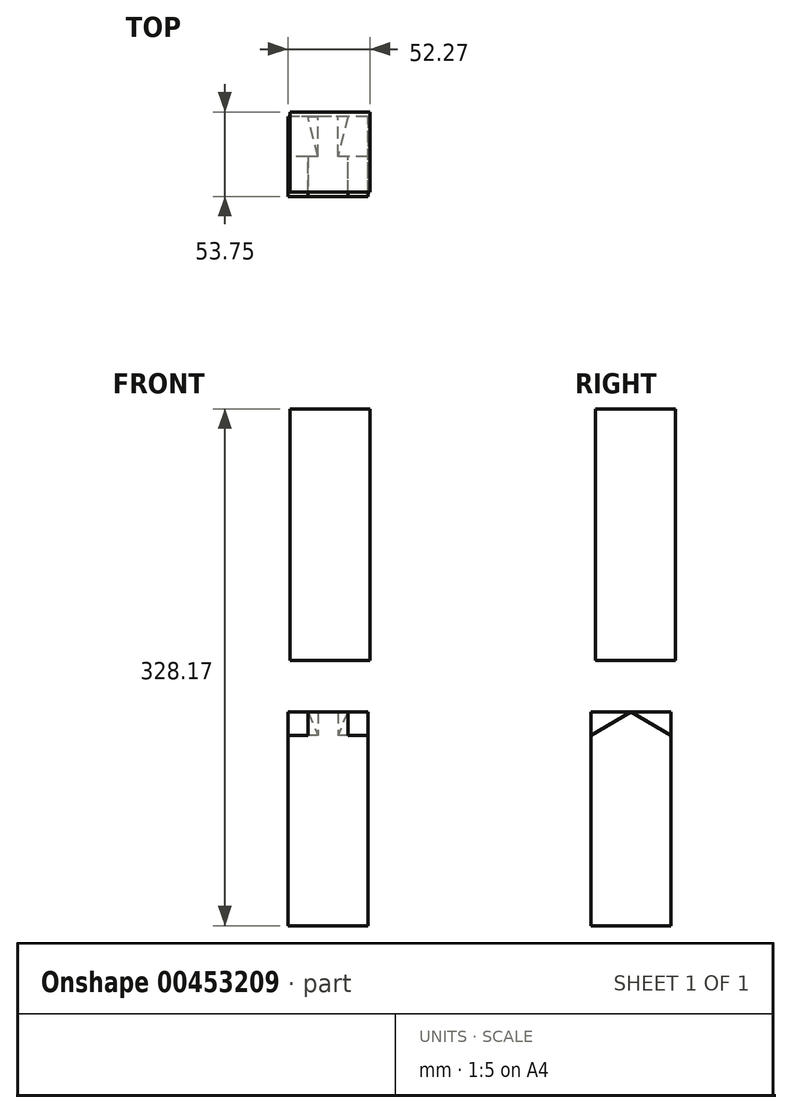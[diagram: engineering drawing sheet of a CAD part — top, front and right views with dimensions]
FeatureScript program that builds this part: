
annotation { "Feature Type Name" : "Feature", "Feature Type Description" : "" }
export const myFeature = defineFeature(function(context is Context, id is Id, definition is map)
    precondition{}
    {
        {
            var Q0;
            Q0=qCreatedBy(makeId("Top.planeOp"),FACE);
            var sketch = newSketch(context, id + "F0", { "sketchPlane" : qUnion([Q0])});
            skLineSegment(sketch, "E0.bottom", {"start": v(30.23, -20.65) * mm, "end": v(-20.57, -20.65) * mm});
            skLineSegment(sketch, "E0.top", {"start": v(30.23, 30.15) * mm, "end": v(-20.57, 30.15) * mm});
            skLineSegment(sketch, "E0.left", {"start": v(30.23, -20.65) * mm, "end": v(30.23, 30.15) * mm});
            skLineSegment(sketch, "E0.right", {"start": v(-20.57, -20.65) * mm, "end": v(-20.57, 30.15) * mm});
            skSolve(sketch);
        }
        {
            var Q0;
            Q0=makeQuery(id+"F0.imprint","IMPRINT",FACE,{"disambiguationData":[TD([[makeQuery(id+"F0.imprint","IMPRINT",EDGE,{"derivedFrom":sQuery(id+"F0.wireOp",EDGE,"E0.bottom")}),-1.0]])]});
            extrude(context, id + "F1", {"entities" : qUnion([Q0]), "depth" : 135.89 * mm});
        }
        {
            var Q0;
            Q0=makeQuery(id+"F1.opExtrude","SWEPT_FACE",FACE,{"disambiguationData":[OSD([sQuery(id+"F0.wireOp",EDGE,"E0.top")])]});
            var sketch = newSketch(context, id + "F2", { "sketchPlane" : qUnion([Q0])});
            skLineSegment(sketch, "E1", {"start": v(-17.53, 135.9) * mm, "end": v(-11.18, 120.72) * mm});
            skLineSegment(sketch, "E2", {"start": v(7.87, 135.9) * mm, "end": v(1.52, 120.72) * mm});
            skLineSegment(sketch, "E3", {"start": v(-11.18, 120.72) * mm, "end": v(1.52, 120.72) * mm});
            skLineSegment(sketch, "E4", {"start": v(-11.18, 120.72) * mm, "end": v(-30.23, 120.72) * mm});
            skLineSegment(sketch, "E5", {"start": v(1.52, 120.72) * mm, "end": v(20.57, 120.72) * mm});
            skSolve(sketch);
        }
        {
            var Q0;
            Q0=makeQuery(id+"F1.opExtrude","SWEPT_FACE",FACE,{"disambiguationData":[OSD([sQuery(id+"F0.wireOp",EDGE,"E0.right")])]});
            var sketch = newSketch(context, id + "F3", { "sketchPlane" : qUnion([Q0])});
            skLineSegment(sketch, "E6", {"start": v(-30.15, 120.72) * mm, "end": v(-4.75, 135.9) * mm});
            skLineSegment(sketch, "E7", {"start": v(-4.75, 135.9) * mm, "end": v(20.65, 120.72) * mm});
            skSolve(sketch);
        }
        {
            var Q0;
            Q0=makeQuery(id+"F1.opExtrude","CAP_FACE",FACE,{"disambiguationData":[OSD([sQuery(id+"F0.wireOp",EDGE,"E0.bottom"),sQuery(id+"F0.wireOp",EDGE,"E0.top"),sQuery(id+"F0.wireOp",EDGE,"E0.left"),sQuery(id+"F0.wireOp",EDGE,"E0.right")])],"isStart":false});
            var sketch = newSketch(context, id + "F4", { "sketchPlane" : qUnion([Q0])});
            skLineSegment(sketch, "E8", {"start": v(-7.87, 30.15) * mm, "end": v(-7.87, -20.65) * mm});
            skLineSegment(sketch, "E9", {"start": v(17.53, 30.15) * mm, "end": v(17.53, -20.65) * mm});
            skLineSegment(sketch, "E10", {"start": v(-20.57, 4.75) * mm, "end": v(30.23, 4.75) * mm});
            skLineSegment(sketch, "E11", {"start": v(17.53, 30.15) * mm, "end": v(11.18, 4.75) * mm});
            skLineSegment(sketch, "E12", {"start": v(11.18, 4.75) * mm, "end": v(-1.52, 4.75) * mm});
            skLineSegment(sketch, "E13", {"start": v(-1.52, 4.75) * mm, "end": v(-7.87, 30.15) * mm});
            skLineSegment(sketch, "E14", {"start": v(11.18, 4.75) * mm, "end": v(30.23, 4.75) * mm});
            skLineSegment(sketch, "E15", {"start": v(-1.52, 4.75) * mm, "end": v(-20.57, 4.75) * mm});
            skSolve(sketch);
        }
        {
            var Q0;
            {var subQ4=sQuery(id+"F3.wireOp",EDGE,"E6");Q0=makeQuery(id+"F3.imprint","IMPRINT",FACE,{"disambiguationData":[TD([[makeQuery(id+"F3.imprint","IMPRINT",EDGE,{"derivedFrom":subQ4}),-1.0]])]});}
            var sketch = newSketch(context, id + "F5", { "sketchPlane" : qUnion([Q0])});
            skLineSegment(sketch, "E16", {"start": v(-4.75, 135.9) * mm, "end": v(-4.75, 120.72) * mm});
            skLineSegment(sketch, "E17", {"start": v(-4.75, 120.72) * mm, "end": v(-30.15, 120.72) * mm});
            skLineSegment(sketch, "E18", {"start": v(-4.75, 135.9) * mm, "end": v(-30.15, 120.72) * mm});
            skSolve(sketch);
        }
        {
            var Q0;
            Q0=qSketchRegion(id+"F5",true);
            var Q1;
            {var subQ0=sQuery(id+"F3.wireOp",EDGE,"E6");Q1=makeQuery(id+"F3.imprint","IMPRINT",FACE,{"disambiguationData":[TD([[makeQuery(id+"F3.imprint","IMPRINT",EDGE,{"derivedFrom":subQ0}),1.0]])]});}
            extrude(context, id + "F6", {"entities" : qUnion([Q0, Q1]), "operationType" : NewBodyOperationType.REMOVE, "oppositeDirection" : true, "depth" : 50.8 * mm});
        }
        {
            var Q0;
            Q0=makeQuery(id+"F6.boolean.opBoolean","COPY",FACE,{"derivedFrom":makeQuery(id+"F6.opExtrude","SWEPT_FACE",FACE,{"disambiguationData":[OSD([sQuery(id+"F5.wireOp",EDGE,"E16")])]})});
            var sketch = newSketch(context, id + "F7", { "sketchPlane" : qUnion([Q0])});
            skLineSegment(sketch, "E19", {"start": v(-11.18, 135.9) * mm, "end": v(-11.18, 120.72) * mm});
            skSolve(sketch);
        }
        {
            var Q0;
            Q0=makeQuery(id+"F6.boolean.opBoolean","COPY",FACE,{"derivedFrom":makeQuery(id+"F6.opExtrude","SWEPT_FACE",FACE,{"disambiguationData":[OSD([sQuery(id+"F5.wireOp",EDGE,"E17")])]})});
            var sketch = newSketch(context, id + "F8", { "sketchPlane" : qUnion([Q0])});
            skLineSegment(sketch, "E20", {"start": v(11.18, 30.15) * mm, "end": v(11.18, 4.75) * mm});
            skSolve(sketch);
        }
        {
            var Q0;
            {var subQ0=sQuery(id+"F7.wireOp",EDGE,"E19");Q0=makeQuery(id+"F7.imprint","IMPRINT",FACE,{"disambiguationData":[TD([[makeQuery(id+"F7.imprint","IMPRINT",EDGE,{"derivedFrom":subQ0}),1.0]])]});}
            var sketch = newSketch(context, id + "F9", { "sketchPlane" : qUnion([Q0])});
            skLineSegment(sketch, "E21", {"start": v(1.52, 135.9) * mm, "end": v(1.52, 120.72) * mm});
            skSolve(sketch);
        }
        {
            var Q0;
            {var subQ0=sQuery(id+"F8.wireOp",EDGE,"E20");Q0=makeQuery(id+"F8.imprint","IMPRINT",FACE,{"disambiguationData":[TD([[makeQuery(id+"F8.imprint","IMPRINT",EDGE,{"derivedFrom":subQ0}),-1.0]])]});}
            var sketch = newSketch(context, id + "F10", { "sketchPlane" : qUnion([Q0])});
            skLineSegment(sketch, "E22", {"start": v(-1.52, 4.75) * mm, "end": v(-1.52, 30.15) * mm});
            skSolve(sketch);
        }
        {
            var Q0;
            {var subQ0=sQuery(id+"F2.wireOp",EDGE,"E1");Q0=makeQuery(id+"F2.imprint","IMPRINT",FACE,{"disambiguationData":[TD([[makeQuery(id+"F2.imprint","IMPRINT",EDGE,{"derivedFrom":subQ0}),1.0]])]});}
            var sketch = newSketch(context, id + "F11", { "sketchPlane" : qUnion([Q0])});
            skLineSegment(sketch, "E23", {"start": v(-11.18, 135.9) * mm, "end": v(1.52, 135.9) * mm});
            skLineSegment(sketch, "E24", {"start": v(1.52, 135.9) * mm, "end": v(1.52, 120.72) * mm});
            skLineSegment(sketch, "E25", {"start": v(1.52, 120.72) * mm, "end": v(-11.18, 120.72) * mm});
            skLineSegment(sketch, "E26", {"start": v(-11.18, 120.72) * mm, "end": v(-11.18, 135.9) * mm});
            skSolve(sketch);
        }
        {
            var Q0;
            Q0=makeQuery(id+"F11.imprint","IMPRINT",FACE,{"disambiguationData":[TD([[makeQuery(id+"F11.imprint","IMPRINT",EDGE,{"derivedFrom":sQuery(id+"F11.wireOp",EDGE,"E23")}),-1.0]])]});
            extrude(context, id + "F12", {"entities" : qUnion([Q0]), "operationType" : NewBodyOperationType.ADD, "oppositeDirection" : true, "depth" : 27.71 * mm});
        }
        {
            var Q0;
            {var subQ0=sQuery(id+"F2.wireOp",EDGE,"E1");Q0=makeQuery(id+"F2.imprint","IMPRINT",FACE,{"disambiguationData":[TD([[makeQuery(id+"F2.imprint","IMPRINT",EDGE,{"derivedFrom":subQ0}),1.0]])]});}
            extrude(context, id + "F13", {"entities" : qUnion([Q0]), "operationType" : NewBodyOperationType.ADD, "oppositeDirection" : true, "depth" : 36.9 * mm});
        }
        {
            var Q0;
            {var subQ0=sQuery(id+"F4.wireOp",EDGE,"E11");Q0=makeQuery(id+"F4.imprint","IMPRINT",FACE,{"disambiguationData":[TD([[makeQuery(id+"F4.imprint","IMPRINT",EDGE,{"derivedFrom":subQ0}),1.0]])]});}
            extrude(context, id + "F14", {"entities" : qUnion([Q0]), "operationType" : NewBodyOperationType.REMOVE, "endBound" : BoundingType.UP_TO_NEXT, "oppositeDirection" : true, "depth" : 14.83 * mm});
        }
        {
            var Q0;
            Q0=sQuery(id+"F7.wireOp",VERTEX,"E19.start");
            var Q1;
            Q1=sQuery(id+"F8.wireOp",VERTEX,"E20.start");
            var Q2;
            {var subQ0=sQuery(id+"F2.wireOp",EDGE,"E1");Q2=makeQuery(id+"F14.boolean.opBoolean","MERGE",VERTEX,{"derivedFrom":[makeQuery(id+"F13.opExtrude","CAP_VERTEX",VERTEX,{"disambiguationData":[OSD([sQuery(id+"F0.wireOp",EDGE,"E0.top"),subQ0])],"isStart":true}),makeQuery(id+"F14.opExtrude","CAP_VERTEX",VERTEX,{"disambiguationData":[OSD([subQ0,sQuery(id+"F4.wireOp",EDGE,"E9"),sQuery(id+"F4.wireOp",EDGE,"E11"),sQuery(id+"F4.wireOp",EDGE,"E14")])],"isStart":false})]});}
            cPlane(context, id + "F15", {"entities" : qUnion([Q0, Q1, Q2]), "cplaneType" : CPlaneType.THREE_POINT, "offset" : 25.4 * mm, "width" : 152.4 * mm, "height" : 152.4 * mm});
        }
        {
            var Q0;
            Q0=qCreatedBy(id+"F15.planeOp",FACE);
            var sketch = newSketch(context, id + "F16", { "sketchPlane" : qUnion([Q0])});
            skLineSegment(sketch, "E27", {"start": v(-21.22, 132.12) * mm, "end": v(4.84, 129.67) * mm});
            skLineSegment(sketch, "E28", {"start": v(3.53, 115.68) * mm, "end": v(-21.22, 115.68) * mm});
            skLineSegment(sketch, "E29", {"start": v(-21.22, 115.68) * mm, "end": v(-21.22, 132.12) * mm});
            skLineSegment(sketch, "E30", {"start": v(4.84, 129.67) * mm, "end": v(3.53, 115.68) * mm});
            skSolve(sketch);
        }
        {
            var Q0;
            Q0=qSketchRegion(id+"F16",true);
            extrude(context, id + "F17", {"entities" : qUnion([Q0]), "operationType" : NewBodyOperationType.REMOVE, "oppositeDirection" : true, "depth" : 5.82 * mm});
        }
        {
            var Q0;
            Q0=makeQuery(id+"F1.opExtrude","SWEPT_FACE",FACE,{"disambiguationData":[OSD([sQuery(id+"F0.wireOp",EDGE,"E0.left")])]});
            extrude(context, id + "F18", {"entities" : qUnion([Q0]), "operationType" : NewBodyOperationType.ADD, "oppositeDirection" : true, "depth" : 25.65 * mm});
        }
        {
            var Q0;
            Q0=makeQuery(id+"F1.opExtrude","SWEPT_FACE",FACE,{"disambiguationData":[OSD([sQuery(id+"F0.wireOp",EDGE,"E0.left")])]});
            var sketch = newSketch(context, id + "F19", { "sketchPlane" : qUnion([Q0])});
            skLineSegment(sketch, "E31", {"start": v(4.75, 135.9) * mm, "end": v(4.75, 120.72) * mm});
            skLineSegment(sketch, "E32", {"start": v(4.75, 120.72) * mm, "end": v(30.15, 120.72) * mm});
            skLineSegment(sketch, "E33", {"start": v(30.15, 120.72) * mm, "end": v(4.75, 135.9) * mm});
            skSolve(sketch);
        }
        {
            var Q0;
            Q0=makeQuery(id+"F19.imprint","IMPRINT",FACE,{"disambiguationData":[TD([[makeQuery(id+"F19.imprint","IMPRINT",EDGE,{"derivedFrom":sQuery(id+"F19.wireOp",EDGE,"E31")}),1.0]])]});
            extrude(context, id + "F20", {"entities" : qUnion([Q0]), "operationType" : NewBodyOperationType.ADD, "oppositeDirection" : true, "depth" : 50.8 * mm});
        }
        {
            var Q0;
            Q0=sQuery(id+"F9.wireOp",VERTEX,"E21.start");
            var Q1;
            Q1=makeQuery(id+"F13.opExtrude","CAP_VERTEX",VERTEX,{"disambiguationData":[OSD([sQuery(id+"F0.wireOp",EDGE,"E0.top"),sQuery(id+"F2.wireOp",EDGE,"E2")])],"isStart":true});
            var Q2;
            Q2=sQuery(id+"F10.wireOp",VERTEX,"E22.end");
            cPlane(context, id + "F21", {"entities" : qUnion([Q0, Q1, Q2]), "cplaneType" : CPlaneType.THREE_POINT, "offset" : 25.4 * mm, "width" : 152.4 * mm, "height" : 152.4 * mm});
        }
        {
            var Q0;
            Q0=qCreatedBy(id+"F21.planeOp",FACE);
            var sketch = newSketch(context, id + "F22", { "sketchPlane" : qUnion([Q0])});
            skLineSegment(sketch, "E34", {"start": v(19.22, 128.42) * mm, "end": v(19.22, 111.94) * mm});
            skLineSegment(sketch, "E35", {"start": v(-6.85, 125.94) * mm, "end": v(19.22, 128.42) * mm});
            skLineSegment(sketch, "E36", {"start": v(-6.85, 125.94) * mm, "end": v(-5.53, 111.94) * mm});
            skLineSegment(sketch, "E37", {"start": v(-5.53, 111.94) * mm, "end": v(19.22, 111.94) * mm});
            skSolve(sketch);
        }
        {
            var Q0;
            Q0=makeQuery(id+"F22.imprint","IMPRINT",FACE,{"disambiguationData":[TD([[makeQuery(id+"F22.imprint","IMPRINT",EDGE,{"derivedFrom":sQuery(id+"F22.wireOp",EDGE,"E34")}),-1.0]])]});
            extrude(context, id + "F23", {"entities" : qUnion([Q0]), "operationType" : NewBodyOperationType.REMOVE, "oppositeDirection" : true, "depth" : 9.9 * mm});
        }
        {
            var Q0;
            Q0=makeQuery(id+"F1.opExtrude","SWEPT_FACE",FACE,{"disambiguationData":[OSD([sQuery(id+"F0.wireOp",EDGE,"E0.right")])]});
            extrude(context, id + "F24", {"entities" : qUnion([Q0]), "operationType" : NewBodyOperationType.ADD, "oppositeDirection" : true, "depth" : 28.2 * mm});
        }
        {
            var Q0;
            {var subQ0=sQuery(id+"F0.wireOp",EDGE,"E0.top");Q0=makeQuery(id+"F13.boolean.opBoolean","MERGE",FACE,{"derivedFrom":[makeQuery(id+"F12.boolean.opBoolean","MERGE",FACE,{"derivedFrom":[makeQuery(id+"F1.opExtrude","CAP_FACE",FACE,{"disambiguationData":[OSD([sQuery(id+"F0.wireOp",EDGE,"E0.bottom"),subQ0,sQuery(id+"F0.wireOp",EDGE,"E0.left"),sQuery(id+"F0.wireOp",EDGE,"E0.right")])],"isStart":false}),makeQuery(id+"F12.opExtrude","SWEPT_FACE",FACE,{"disambiguationData":[OSD([sQuery(id+"F11.wireOp",EDGE,"E23")])]})]}),makeQuery(id+"F13.opExtrude","SWEPT_FACE",FACE,{"disambiguationData":[OSD([subQ0])]})]});}
            var sketch = newSketch(context, id + "F25", { "sketchPlane" : qUnion([Q0])});
            skLineSegment(sketch, "E38", {"start": v(-1.52, 4.75) * mm, "end": v(-7.87, 4.75) * mm});
            skLineSegment(sketch, "E39", {"start": v(-7.87, 4.75) * mm, "end": v(-7.87, 29.86) * mm});
            skSolve(sketch);
        }
        {
            var Q0;
            Q0=makeQuery(id+"F25.imprint","IMPRINT",FACE,{"disambiguationData":[TD([[makeQuery(id+"F25.imprint","IMPRINT",EDGE,{"derivedFrom":sQuery(id+"F25.wireOp",EDGE,"E38")}),-1.0]])]});
            extrude(context, id + "F26", {"entities" : qUnion([Q0]), "operationType" : NewBodyOperationType.REMOVE, "oppositeDirection" : true, "depth" : 3.56 * mm});
        }
        {
            var Q0;
            Q0=makeQuery(id+"F20.boolean.opBoolean","MERGE",FACE,{"derivedFrom":[makeQuery(id+"F1.opExtrude","SWEPT_FACE",FACE,{"disambiguationData":[OSD([sQuery(id+"F0.wireOp",EDGE,"E0.right")])]}),makeQuery(id+"F20.opExtrude","CAP_FACE",FACE,{"disambiguationData":[OSD([sQuery(id+"F19.wireOp",EDGE,"E31"),sQuery(id+"F19.wireOp",EDGE,"E32"),sQuery(id+"F19.wireOp",EDGE,"E33")])],"isStart":false})]});
            extrude(context, id + "F27", {"entities" : qUnion([Q0]), "operationType" : NewBodyOperationType.ADD, "oppositeDirection" : true, "depth" : 33.53 * mm});
        }
        {
            var Q0;
            Q0=makeQuery(id+"F20.boolean.opBoolean","MERGE",FACE,{"derivedFrom":[makeQuery(id+"F1.opExtrude","SWEPT_FACE",FACE,{"disambiguationData":[OSD([sQuery(id+"F0.wireOp",EDGE,"E0.left")])]}),makeQuery(id+"F20.opExtrude","CAP_FACE",FACE,{"disambiguationData":[OSD([sQuery(id+"F19.wireOp",EDGE,"E31"),sQuery(id+"F19.wireOp",EDGE,"E32"),sQuery(id+"F19.wireOp",EDGE,"E33")])],"isStart":true})]});
            var sketch = newSketch(context, id + "F28", { "sketchPlane" : qUnion([Q0])});
            skLineSegment(sketch, "E40", {"start": v(30.15, 120.72) * mm, "end": v(-20.65, 120.72) * mm});
            skLineSegment(sketch, "E41", {"start": v(-20.65, 120.72) * mm, "end": v(4.75, 135.9) * mm});
            skLineSegment(sketch, "E42", {"start": v(4.75, 135.9) * mm, "end": v(30.15, 120.72) * mm});
            skSolve(sketch);
        }
        {
            var Q0;
            {var subQ0=sQuery(id+"F28.wireOp",EDGE,"E41");Q0=makeQuery(id+"F28.imprint","IMPRINT",FACE,{"disambiguationData":[TD([[makeQuery(id+"F28.imprint","IMPRINT",EDGE,{"derivedFrom":subQ0}),1.0]])]});}
            extrude(context, id + "F29", {"entities" : qUnion([Q0]), "operationType" : NewBodyOperationType.REMOVE, "oppositeDirection" : true, "depth" : 12.7 * mm});
        }
        {
            var Q0;
            Q0=makeQuery(id+"F20.boolean.opBoolean","MERGE",FACE,{"derivedFrom":[makeQuery(id+"F1.opExtrude","SWEPT_FACE",FACE,{"disambiguationData":[OSD([sQuery(id+"F0.wireOp",EDGE,"E0.right")])]}),makeQuery(id+"F20.opExtrude","CAP_FACE",FACE,{"disambiguationData":[OSD([sQuery(id+"F19.wireOp",EDGE,"E31"),sQuery(id+"F19.wireOp",EDGE,"E32"),sQuery(id+"F19.wireOp",EDGE,"E33")])],"isStart":false})]});
            var sketch = newSketch(context, id + "F30", { "sketchPlane" : qUnion([Q0])});
            skLineSegment(sketch, "E43", {"start": v(-30.15, 120.72) * mm, "end": v(20.65, 120.72) * mm});
            skLineSegment(sketch, "E44", {"start": v(-4.75, 135.9) * mm, "end": v(20.65, 120.72) * mm});
            skSolve(sketch);
        }
        {
            var Q0;
            {var subQ0=sQuery(id+"F30.wireOp",EDGE,"E44");Q0=makeQuery(id+"F30.imprint","IMPRINT",FACE,{"disambiguationData":[TD([[makeQuery(id+"F30.imprint","IMPRINT",EDGE,{"derivedFrom":subQ0}),1.0]])]});}
            extrude(context, id + "F31", {"entities" : qUnion([Q0]), "operationType" : NewBodyOperationType.REMOVE, "oppositeDirection" : true, "depth" : 12.7 * mm});
        }
        {
            var Q0;
            Q0=qCreatedBy(makeId("Top.planeOp"),FACE);
            var sketch = newSketch(context, id + "F32", { "sketchPlane" : qUnion([Q0])});
            skLineSegment(sketch, "E45.bottom", {"start": v(-168.45, 33.1) * mm, "end": v(-117.65, 33.1) * mm});
            skLineSegment(sketch, "E45.top", {"start": v(-168.45, -17.7) * mm, "end": v(-117.65, -17.7) * mm});
            skLineSegment(sketch, "E45.left", {"start": v(-168.45, 33.1) * mm, "end": v(-168.45, -17.7) * mm});
            skLineSegment(sketch, "E45.right", {"start": v(-117.65, 33.1) * mm, "end": v(-117.65, -17.7) * mm});
            skSolve(sketch);
        }
        {
            var Q0;
            Q0 = qSketchRegion(id + "F32", true);
            var Q1;
            Q1=makeQuery(id+"F32.imprint","IMPRINT",FACE,{"disambiguationData":[TD([[makeQuery(id+"F32.imprint","IMPRINT",EDGE,{"derivedFrom":sQuery(id+"F32.wireOp",EDGE,"E45.bottom")}),-1.0]])]});
            extrude(context, id + "F33", {"entities" : qUnion([Q0, Q1]), "depth" : 159.77 * mm});
        }
        {
            var Q0;
            Q0=makeQuery(id+"F33.opExtrude","SWEPT_BODY",BODY,{"disambiguationData":[OSD([sQuery(id+"F32.wireOp",EDGE,"E45.bottom"),sQuery(id+"F32.wireOp",EDGE,"E45.top"),sQuery(id+"F32.wireOp",EDGE,"E45.left"),sQuery(id+"F32.wireOp",EDGE,"E45.right")])]});
            transform(context, id + "F34", {"entities" : qUnion([Q0]), "transformType" : TransformType.TRANSLATION_3D, "dx" : 149.35 * mm, "dy" : 0 * mm, "dz" : 168.4 * mm, "makeCopy" : false});
        }
    });
